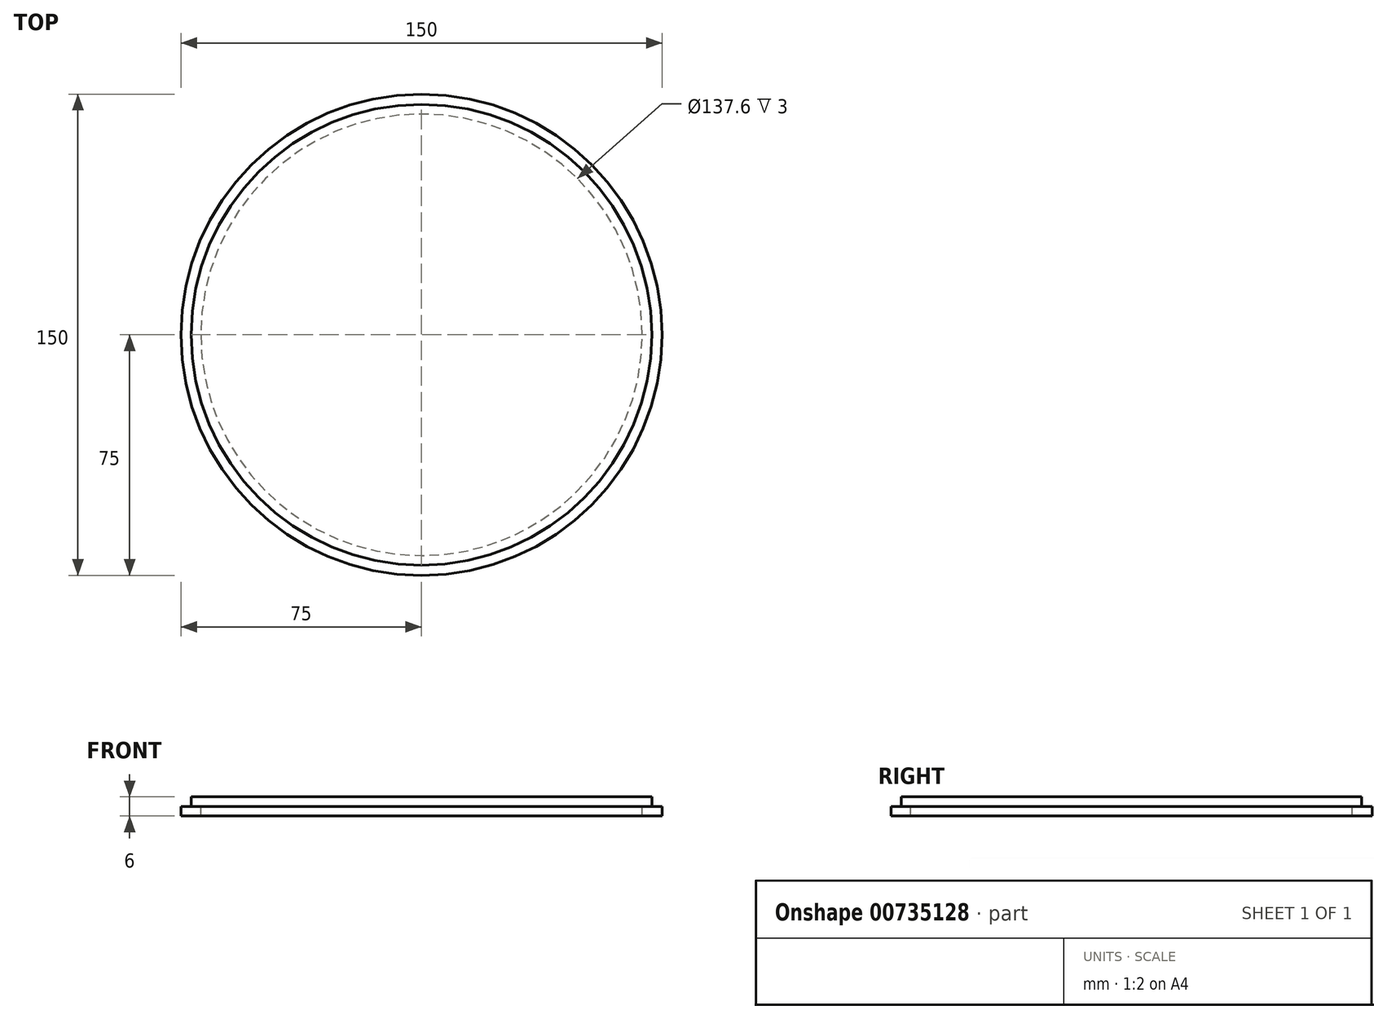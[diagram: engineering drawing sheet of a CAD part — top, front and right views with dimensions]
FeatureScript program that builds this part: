
annotation { "Feature Type Name" : "Feature", "Feature Type Description" : "" }
export const myFeature = defineFeature(function(context is Context, id is Id, definition is map)
    precondition{}
    {
        {
            var Q0;
            Q0=qCreatedBy(makeId("Front.planeOp"),FACE);
            var sketch = newSketch(context, id + "F0", { "sketchPlane" : qUnion([Q0])});
            skLineSegment(sketch, "E0", {"start": v(-75, 0) * mm, "end": v(-75, 3) * mm});
            skLineSegment(sketch, "E1", {"start": v(-75, 3) * mm, "end": v(-71.8, 3) * mm});
            skLineSegment(sketch, "E2", {"start": v(-71.8, 3) * mm, "end": v(-71.8, 6) * mm});
            skLineSegment(sketch, "E3", {"start": v(-75, 0) * mm, "end": v(-68.8, 0) * mm});
            skLineSegment(sketch, "E4", {"start": v(-68.8, 0) * mm, "end": v(-68.8, 3) * mm});
            skLineSegment(sketch, "E5", {"start": v(-68.8, 3) * mm, "end": v(0, 3) * mm});
            skLineSegment(sketch, "E6", {"start": v(-71.8, 6) * mm, "end": v(0, 6) * mm});
            skLineSegment(sketch, "E7", {"start": v(0, 6) * mm, "end": v(0, 3) * mm});
            skSolve(sketch);
        }
        {
            var Q0;
            Q0=makeQuery(id+"F0.imprint","IMPRINT",FACE,{"disambiguationData":[TD([[makeQuery(id+"F0.imprint","IMPRINT",EDGE,{"derivedFrom":sQuery(id+"F0.wireOp",EDGE,"E0")}),-1.0]])]});
            var Q1;
            Q1=sQuery(id+"F0.wireOp",EDGE,"E7");
            revolve(context, id + "F1", {"surfaceOperationType" : NewSurfaceOperationType.NEW, "entities" : qUnion([Q0]), "axis" : qUnion([Q1]), "revolveType" : RevolveType.FULL});
        }
    });
